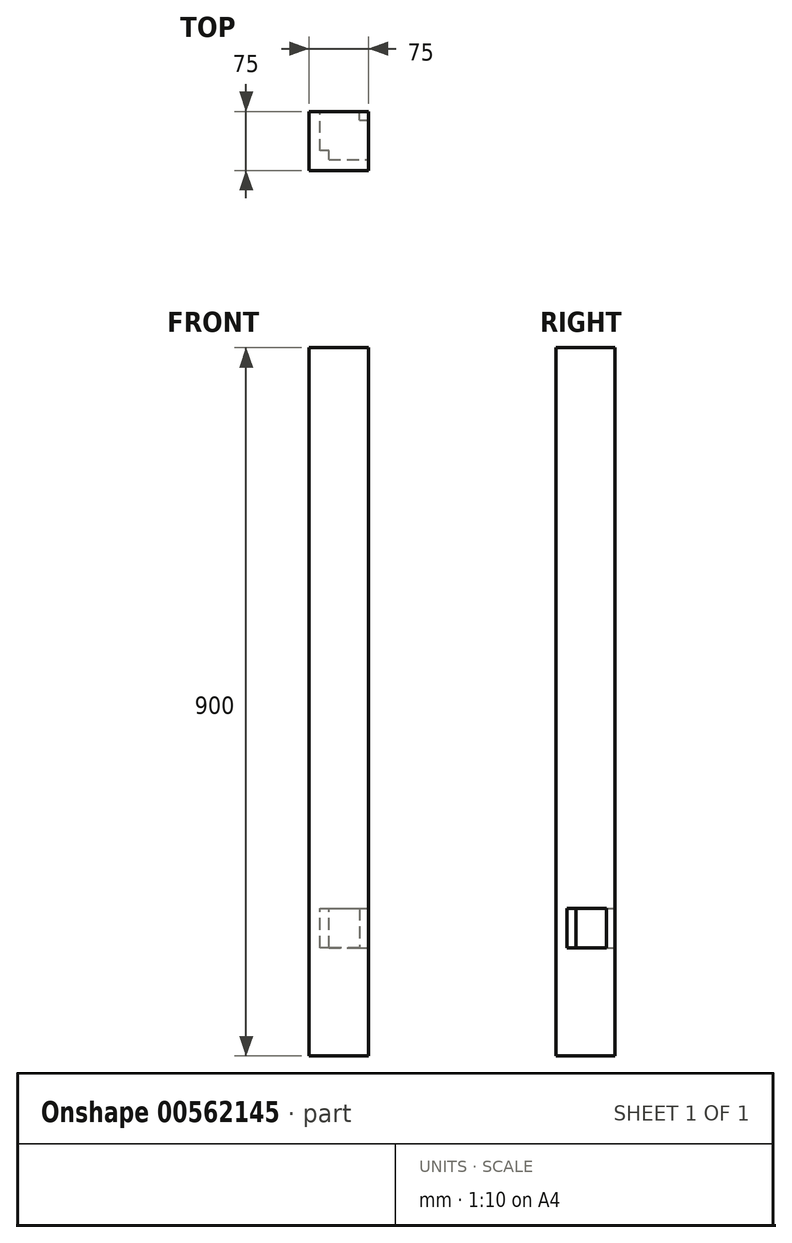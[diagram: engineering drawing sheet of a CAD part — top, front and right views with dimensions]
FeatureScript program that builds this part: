
annotation { "Feature Type Name" : "Feature", "Feature Type Description" : "" }
export const myFeature = defineFeature(function(context is Context, id is Id, definition is map)
    precondition{}
    {
        {
            var Q0;
            Q0=qCreatedBy(makeId("Top.planeOp"),FACE);
            var sketch = newSketch(context, id + "F0", { "sketchPlane" : qUnion([Q0])});
            skLineSegment(sketch, "E0.bottom", {"start": v(37.5, 37.5) * mm, "end": v(-37.5, 37.5) * mm});
            skLineSegment(sketch, "E0.top", {"start": v(37.5, -37.5) * mm, "end": v(-37.5, -37.5) * mm});
            skLineSegment(sketch, "E0.left", {"start": v(37.5, 37.5) * mm, "end": v(37.5, -37.5) * mm});
            skLineSegment(sketch, "E0.right", {"start": v(-37.5, 37.5) * mm, "end": v(-37.5, -37.5) * mm});
            skPoint(sketch, "E0.middle", {"position": v(0, 0) * mm});
            skSolve(sketch);
        }
        {
            var Q0;
            Q0 = qSketchRegion(id + "F0", true);
            extrude(context, id + "F1", {"entities" : qUnion([Q0]), "depth" : 900 * mm, "offsetDistance" : 25 * mm});
        }
        {
            var Q0;
            Q0=makeQuery(id+"F1.opExtrude","SWEPT_FACE",FACE,{"disambiguationData":[OSD([sQuery(id+"F0.wireOp",EDGE,"E0.left")])]});
            var sketch = newSketch(context, id + "F2", { "sketchPlane" : qUnion([Q0])});
            skLineSegment(sketch, "E1", {"start": v(-37.5, 0) * mm, "end": v(-37.5, 125) * mm});
            skLineSegment(sketch, "E2", {"start": v(-37.5, 125) * mm, "end": v(-37.5, 137.5) * mm});
            skLineSegment(sketch, "E3", {"start": v(-37.5, 137.5) * mm, "end": v(-23.5, 137.5) * mm});
            skLineSegment(sketch, "E4", {"start": v(-23.5, 137.5) * mm, "end": v(26.5, 137.5) * mm});
            skLineSegment(sketch, "E5", {"start": v(26.5, 137.5) * mm, "end": v(26.5, 187.5) * mm});
            skLineSegment(sketch, "E6", {"start": v(26.5, 187.5) * mm, "end": v(-23.5, 187.5) * mm});
            skLineSegment(sketch, "E7", {"start": v(-23.5, 187.5) * mm, "end": v(-23.5, 137.5) * mm});
            skPoint(sketch, "E8.start.orphan", {"position": v(-23.5, 77.5) * mm});
            skPoint(sketch, "E9.end.orphan", {"position": v(26.5, 127.5) * mm});
            skPoint(sketch, "E9.start.orphan", {"position": v(-23.5, 127.5) * mm});
            skLineSegment(sketch, "E10", {"start": v(-37.5, 125) * mm, "end": v(-37.5, 200) * mm});
            skLineSegment(sketch, "E11", {"start": v(-37.5, 200) * mm, "end": v(37.5, 200) * mm});
            skSolve(sketch);
        }
        {
            var Q0;
            Q0 = qSketchRegion(id + "F2", true);
            extrude(context, id + "F3", {"entities" : qUnion([Q0]), "operationType" : NewBodyOperationType.REMOVE, "oppositeDirection" : true, "depth" : 50 * mm, "offsetDistance" : 25 * mm});
        }
        {
            var Q0;
            Q0=makeQuery(id+"F1.opExtrude","SWEPT_FACE",FACE,{"disambiguationData":[OSD([sQuery(id+"F0.wireOp",EDGE,"E0.bottom")])]});
            var sketch = newSketch(context, id + "F4", { "sketchPlane" : qUnion([Q0])});
            skSolve(sketch);
        }
        {
            var Q0;
            {var subQ0=sQuery(id+"F0.wireOp",EDGE,"E0.bottom");Q0=makeQuery(id+"F4.imprint","IMPRINT",FACE,{"disambiguationData":[TD([[makeQuery(id+"F4.imprint","IMPRINT",EDGE,{"derivedFrom":makeQuery(id+"F1.opExtrude","CAP_EDGE",EDGE,{"disambiguationData":[OSD([subQ0])],"isStart":true})}),1.0]])]});}
            var sketch = newSketch(context, id + "F5", { "sketchPlane" : qUnion([Q0])});
            skLineSegment(sketch, "E12", {"start": v(0, 0) * mm, "end": v(-37.5, 0) * mm});
            skLineSegment(sketch, "E13", {"start": v(-37.5, 125) * mm, "end": v(-37.5, 137.5) * mm});
            skLineSegment(sketch, "E14", {"start": v(-37.5, 137.5) * mm, "end": v(-26.5, 137.5) * mm});
            skLineSegment(sketch, "E15", {"start": v(-26.5, 137.5) * mm, "end": v(23.5, 137.5) * mm});
            skLineSegment(sketch, "E16", {"start": v(23.5, 137.5) * mm, "end": v(23.5, 187.5) * mm});
            skLineSegment(sketch, "E17", {"start": v(23.5, 187.5) * mm, "end": v(-26.5, 187.5) * mm});
            skLineSegment(sketch, "E18", {"start": v(-26.5, 187.5) * mm, "end": v(-26.5, 137.5) * mm});
            skSolve(sketch);
        }
        {
            var Q0;
            Q0 = qSketchRegion(id + "F5", true);
            extrude(context, id + "F6", {"entities" : qUnion([Q0]), "operationType" : NewBodyOperationType.REMOVE, "oppositeDirection" : true, "depth" : 50 * mm, "offsetDistance" : 25 * mm});
        }
    });
